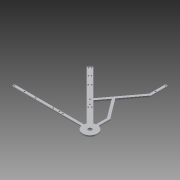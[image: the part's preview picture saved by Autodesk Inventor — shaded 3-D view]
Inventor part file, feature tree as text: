
AUTODESK INVENTOR PART (.ipt)
format: ipt  version: 2013 (Build 170138000, 138)  size: 223,744 bytes
history: native  units: in
note: dims shown in document units (in); Inventor stores cm internally (conversion verified against a paired STEP export)
features: extrude x5, sketch x5, reference x5, projected_geometry x1
ambient origin geometry x8: Origin, YZ Plane, XZ Plane, XY Plane, X Axis, Y Axis, Z Axis, Center Point
bodies: Solid1 (feature_tree)
feature tree (16):
  extrude  "Extrusion1"  Depth=0.25in TaperAngle=0.0deg
  extrude  "Extrusion6"  Depth=0.25in TaperAngle=0.0deg
  extrude  "Extrusion7"  TaperAngle=0.0deg  [1 undecoded]
  extrude  "Extrusion8"  Depth=1.0in TaperAngle=0.0deg
  extrude  "Extrusion9"  Depth=0.25in TaperAngle=0.0deg
  sketch  "Sketch1"  dims[d2=0.5in d3=0.5in d4=1.5in d6=1.5in d7=0.25in d8=0.25in d9=0.25in d10=0.5in d11=0.5in d12=3.75in d13=0.266in d14=0.266in d15=0.266in d16=0.25in d17=0.266in d18=0.25in d19=0.25in d20=0.266in d21=0.266in d22=0.266in d23=0.25in d24=0.266in d25=1.125in d28=1.5in d30=0.25in d31=5.5in d34=0.25in d37=10.926in d38=10.6389in d39=0.2871in d40=0.2871in d41=15.5in d42=15.5in d43=0.25in d44=0.5in d45=0.266in d46=0.25in d47=0.266in d48=0.266in d49=15.5in d50=0.25in d51=0.266in d52=0.25in d54=0.266in d55=0.266in d56=0.266in d57=2.0in d58=2.0in d59=2.0in d60=0.297in d61=0.297in d62=0.297in d63=0.297in d64=2.0in d67=0.25in d68=0.0in]
  sketch  "Sketch7"  dims[d99=0.748in d100=0.25in d101=0.0in]
  sketch  "Sketch9"  dims[d102=0.0in d103=0.0in]
  reference  "Reference6"
  sketch  "Sketch10"  dims[d104=0.0in d105=1.0in d106=0.0in]
  projected_geometry  "Projected Loop2"
  sketch  "Sketch11"  dims[d107=0.5in d109=0.25in d110=0.0in d111=1.0in d112=0.0in]
  reference  "Reference7"
  reference  "Reference8"
  reference  "Reference9"
  reference  "Reference10"
note: 1 required parameter value undecoded (feature->parameter linkage not recoverable at this tier; creation-order binding heuristic only, values carry confidence <= 0.55)
